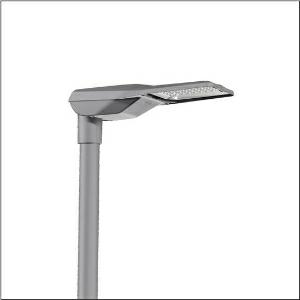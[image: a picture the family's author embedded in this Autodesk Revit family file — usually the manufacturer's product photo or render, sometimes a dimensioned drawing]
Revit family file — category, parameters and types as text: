
# Revit family: streetlight_sl_21_iq_mini___pl52_5xe2h41d08gb_a481
name_source: partatom
category: Lighting Fixtures
units: mm (PartAtom-declared; Revit-internal decimal feet)

## family parameters
Cut with Voids When Loaded = No
Host = Face
Light Source = No
Part Type = Normal
Room Calculation Point = No
Round Connector Dimension = Use Diameter
Shared = No

## types (1)
- --- (1 x LED, 5810 lm, 37.1 W, 4000K)
    Apparent Load = 37 VA
    CIE Flux Codes = 27 59 98 100 100
    Color Rendering = 70
    Color Temperature = 4000K
    Default Elevation = 1800 mm
    Description = Streetlight SL 21 mini, mast luminaire, primary light control with lens, of PMMA, primary optical cover: cover, of toughened safety glass, transparent, light distribution: PL52, light emission: direct distribution, primary light characteristic: asymmetric, installation type: post-top, side-entry, LED, High Power LED, rated luminous flux: 5.810lm, luminous efficacy: 157lm/W, light colour: 740, colour temperature: 4000K, control gear: ECG iQ, control: Auto-Match, Temp-Guard, Lumen-Switch, Night-Set, Smart-Wire, Light-Fading, Desk-Remote (wireless, voltage-free reading and setting of iQ features in the workshop via application-optimized NFC function/RFID function), optimised constant luminous flux control (CLO 2.0), mains connection: 220..240V, AC, 50/60Hz, start of lifetime: 37W, end of lifetime: 39W, reduction: 18W, luminaire housing, of diecast aluminium, powder-coated, Siteco® metallic grey (DB 702S), corrosivity category C5 according to DIN EN ISO 12944, length: 628mm, width: 235mm, height: 110mm, spigot size: 60/76mm (post-top) and 42/60/76mm (side-entry), mast flange for spigot size: 42mm: 5XC10008XM4, 60mm: 5XC10008XM2, 76/60mm: 5XC10108XM1, protection rating (complete): IP66, insulation class (complete): insulation class II (safety insulation), certification: CE, ENEC, VDE, impact resistance: IK09, permissible operating ambient temperature for outdoor applications: -40..+50°C, standard-compliant lighting for roads and squares, packaging unit: 1 piece

Light Distribution: PL52
    Height = 110 mm
    Lamp = 1 x LED
    Lamp Light Flux = 5810 lm
    Lamp Power = 37.1 W
    Lamp count = 1
    Length = 625 mm
    Luminous efficacy = 157 lm/W
    Manufacturer = Siteco
    ModVariant = No
    Model = 5XE2H41D08GB
    Number of Poles = 1
    OnlyDefault = Yes
    Power Factor = 1
    Product Name = Streetlight SL 21 iQ mini | PL52
    Product group = mast luminaire | pylon top
    ProductGroupID = 6100
    Protection Class = Protection class II
    Protection Degree = IP 66
    RLX_Detail_Level = 1
    RlxData = <blob elided: 101753 chars, md5=3d0cae0b>
    Socket = socket
    Standby Power = 0 W
    System Light Flux = 5810 lm
    System Power = 37 W
    Type Comments = factory setting: luminous flux: 100 % | dim-lin: 254 | 385 mA
    Type Image = l_1003519.jpg
    URL = http://relux.com
    VarID = @adj_109493
    Voltage = 0 V
    Weight = 0.00 kg
    Width = 234 mm

## geometry (parser evidence)
native form markers: Blend x4, Sweep x10
no freeform markers — native parametric forms only
